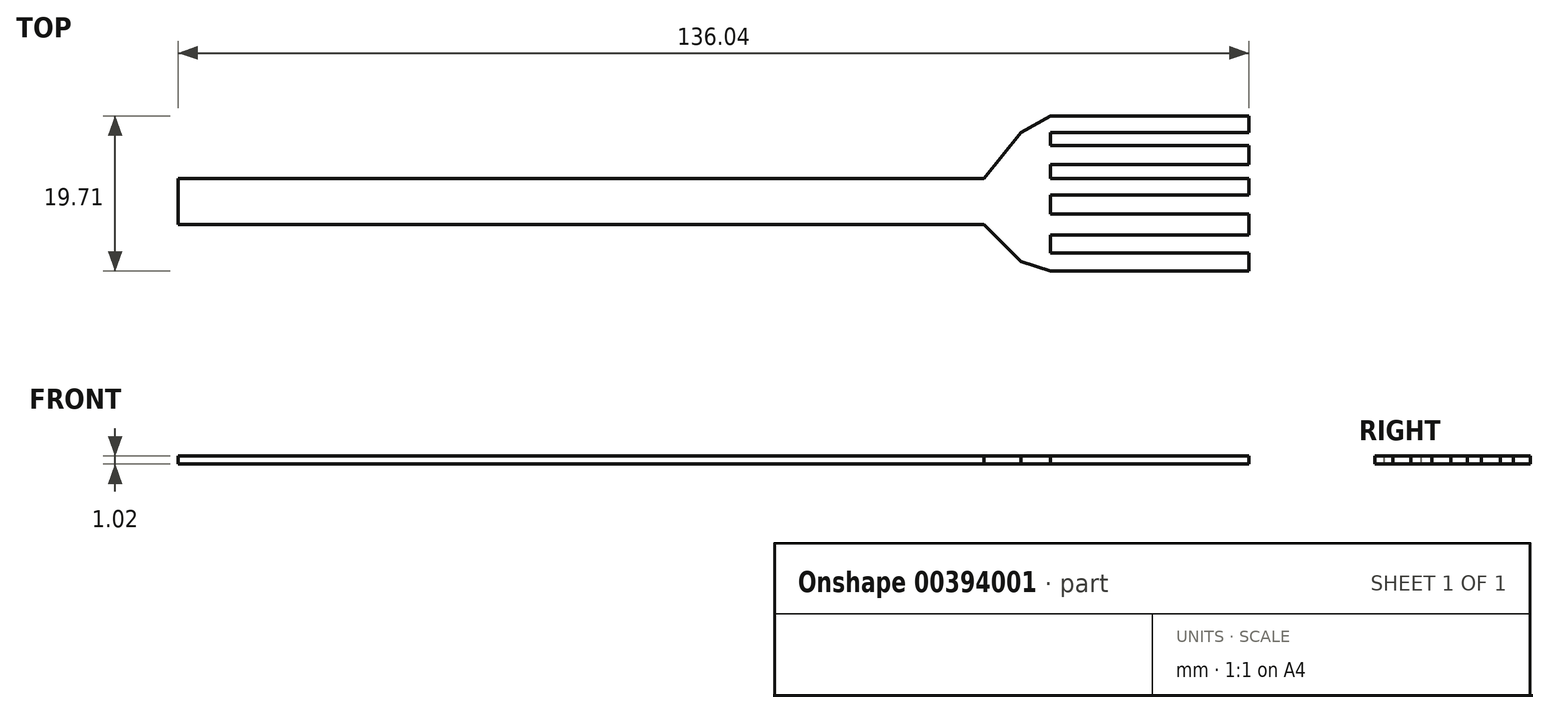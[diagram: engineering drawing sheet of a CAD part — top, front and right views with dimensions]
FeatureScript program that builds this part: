
annotation { "Feature Type Name" : "Feature", "Feature Type Description" : "" }
export const myFeature = defineFeature(function(context is Context, id is Id, definition is map)
    precondition{}
    {
        {
            var Q0;
            Q0=qCreatedBy(makeId("Top.planeOp"),FACE);
            var sketch = newSketch(context, id + "F0", { "sketchPlane" : qUnion([Q0])});
            skLineSegment(sketch, "E0.bottom", {"start": v(0, 0) * mm, "end": v(-102.38, 0) * mm});
            skLineSegment(sketch, "E0.top", {"start": v(0, -5.88) * mm, "end": v(-102.38, -5.88) * mm});
            skLineSegment(sketch, "E0.left", {"start": v(0, 0) * mm, "end": v(0, -5.88) * mm});
            skLineSegment(sketch, "E0.right", {"start": v(-102.38, 0) * mm, "end": v(-102.38, -5.88) * mm});
            skLineSegment(sketch, "E1", {"start": v(0, 0) * mm, "end": v(4.7, 5.8) * mm});
            skLineSegment(sketch, "E2", {"start": v(4.7, 5.8) * mm, "end": v(8.46, 7.95) * mm});
            skLineSegment(sketch, "E3", {"start": v(8.46, 7.95) * mm, "end": v(33.66, 7.95) * mm});
            skLineSegment(sketch, "E4", {"start": v(33.66, 7.95) * mm, "end": v(33.66, 5.8) * mm});
            skLineSegment(sketch, "E5", {"start": v(33.66, 5.8) * mm, "end": v(8.46, 5.8) * mm});
            skLineSegment(sketch, "E6", {"start": v(8.46, 5.8) * mm, "end": v(8.46, 4.2) * mm});
            skLineSegment(sketch, "E7", {"start": v(8.46, 4.2) * mm, "end": v(33.66, 4.2) * mm});
            skLineSegment(sketch, "E8", {"start": v(33.66, 4.2) * mm, "end": v(33.66, 1.78) * mm});
            skLineSegment(sketch, "E9", {"start": v(33.66, 1.78) * mm, "end": v(8.46, 1.78) * mm});
            skLineSegment(sketch, "E10", {"start": v(8.46, 1.78) * mm, "end": v(8.46, 0) * mm});
            skLineSegment(sketch, "E11", {"start": v(8.46, 0) * mm, "end": v(33.66, 0) * mm});
            skLineSegment(sketch, "E12", {"start": v(33.66, 0) * mm, "end": v(33.66, -2.1) * mm});
            skLineSegment(sketch, "E13", {"start": v(33.66, -2.1) * mm, "end": v(8.46, -2.1) * mm});
            skLineSegment(sketch, "E14", {"start": v(8.46, -2.1) * mm, "end": v(8.46, -4.52) * mm});
            skLineSegment(sketch, "E15", {"start": v(8.46, -4.52) * mm, "end": v(33.66, -4.52) * mm});
            skLineSegment(sketch, "E16", {"start": v(33.66, -4.52) * mm, "end": v(33.66, -7.2) * mm});
            skLineSegment(sketch, "E17", {"start": v(33.66, -7.2) * mm, "end": v(8.46, -7.2) * mm});
            skLineSegment(sketch, "E18", {"start": v(8.46, -7.2) * mm, "end": v(8.46, -9.48) * mm});
            skLineSegment(sketch, "E19", {"start": v(8.46, -9.48) * mm, "end": v(33.66, -9.48) * mm});
            skLineSegment(sketch, "E20", {"start": v(33.66, -9.48) * mm, "end": v(33.66, -11.76) * mm});
            skLineSegment(sketch, "E21", {"start": v(33.66, -11.76) * mm, "end": v(8.46, -11.76) * mm});
            skLineSegment(sketch, "E22", {"start": v(8.46, -11.76) * mm, "end": v(4.7, -10.55) * mm});
            skLineSegment(sketch, "E23", {"start": v(4.7, -10.55) * mm, "end": v(0, -5.88) * mm});
            skSolve(sketch);
        }
        {
            var Q0;
            Q0 = qSketchRegion(id + "F0", true);
            extrude(context, id + "F1", {"entities" : qUnion([Q0]), "oppositeDirection" : true, "depth" : 1.02 * mm});
        }
    });
